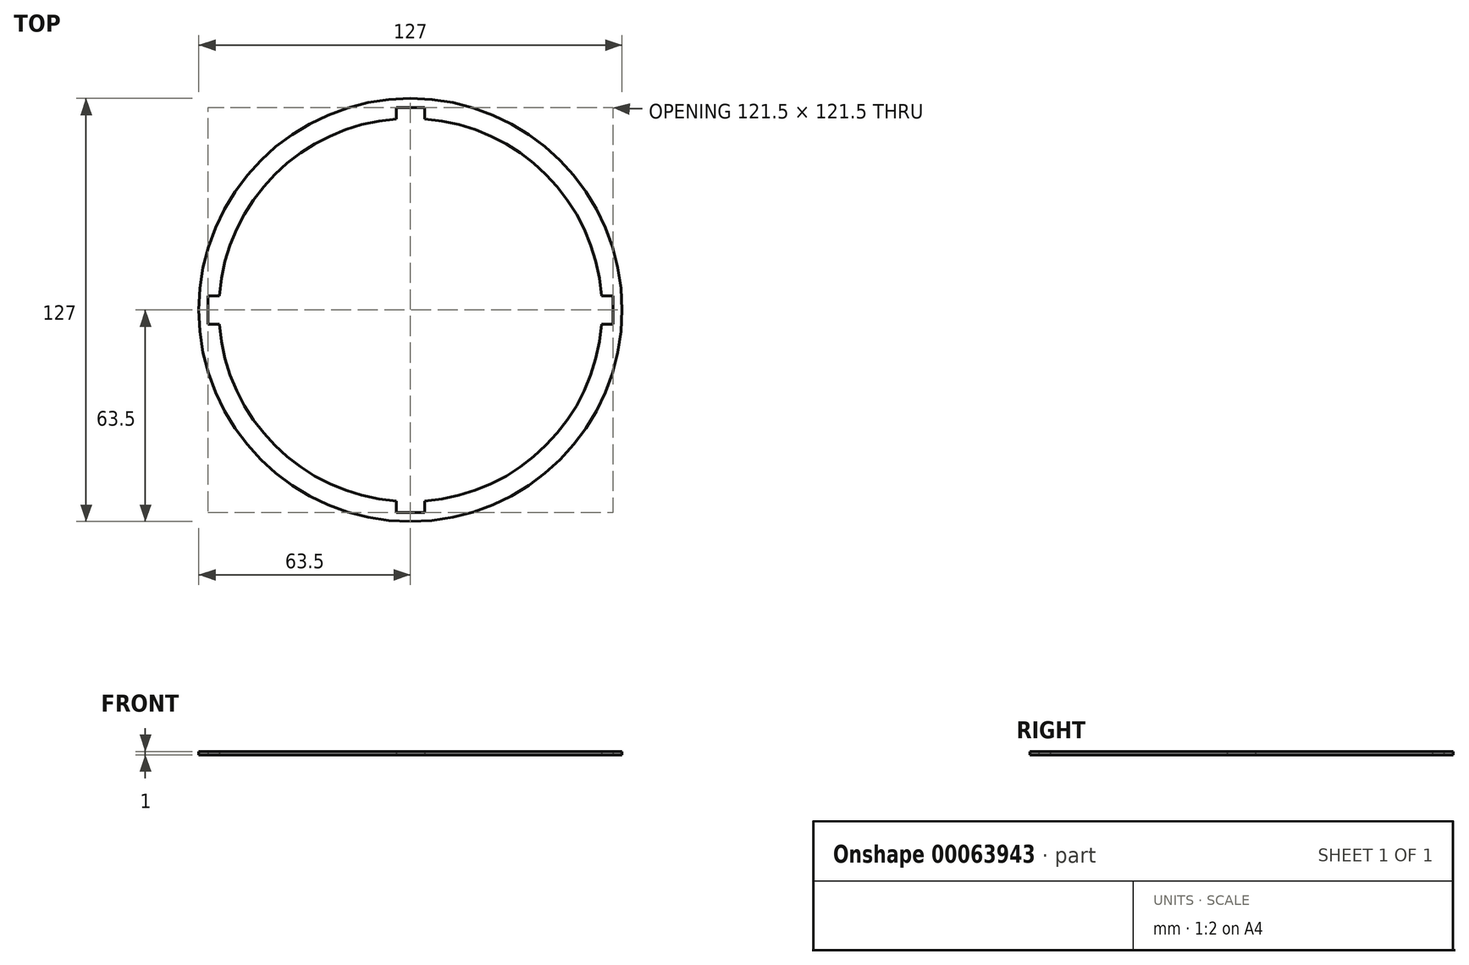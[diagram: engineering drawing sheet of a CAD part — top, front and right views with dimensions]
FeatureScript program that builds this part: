
annotation { "Feature Type Name" : "Feature", "Feature Type Description" : "" }
export const myFeature = defineFeature(function(context is Context, id is Id, definition is map)
    precondition{}
    {
        {
            var Q0;
            Q0=qCreatedBy(makeId("Top.planeOp"),FACE);
            var sketch = newSketch(context, id + "F0", { "sketchPlane" : qUnion([Q0])});
            skCircle(sketch, "E0", {"center": v(0, 0) * mm, "radius": 57.5 * mm});
            skCircle(sketch, "E1", {"center": v(0, 0) * mm, "radius": 63.5 * mm});
            skSolve(sketch);
        }
        {
            var Q0;
            Q0=makeQuery(id+"F0.imprint","IMPRINT",FACE,{"disambiguationData":[TD([[makeQuery(id+"F0.imprint","IMPRINT",EDGE,{"derivedFrom":sQuery(id+"F0.wireOp",EDGE,"E0")}),-1.0]])]});
            extrude(context, id + "F1", {"entities" : qUnion([Q0]), "depth" : 1 * mm});
        }
        {
            var Q0;
            Q0=qCreatedBy(makeId("Top.planeOp"),FACE);
            var sketch = newSketch(context, id + "F2", { "sketchPlane" : qUnion([Q0])});
            skLineSegment(sketch, "E2", {"start": v(0, 60.75) * mm, "end": v(-4.25, 60.75) * mm});
            skLineSegment(sketch, "E3", {"start": v(-4.25, 60.75) * mm, "end": v(-4.25, 56.5) * mm});
            skLineSegment(sketch, "E4", {"start": v(-4.25, 56.5) * mm, "end": v(4.25, 56.5) * mm});
            skLineSegment(sketch, "E5", {"start": v(4.25, 56.5) * mm, "end": v(4.25, 60.75) * mm});
            skLineSegment(sketch, "E6", {"start": v(0, 60.75) * mm, "end": v(4.25, 60.75) * mm});
            skLineSegment(sketch, "E7.MirrorCS", {"start": v(0, -60.75) * mm, "end": v(4.25, -60.75) * mm});
            skLineSegment(sketch, "E8.MirrorCS", {"start": v(0, -60.75) * mm, "end": v(-4.25, -60.75) * mm});
            skLineSegment(sketch, "E9.MirrorCS", {"start": v(4.25, -56.5) * mm, "end": v(4.25, -60.75) * mm});
            skLineSegment(sketch, "E10.MirrorCS", {"start": v(-4.25, -60.75) * mm, "end": v(-4.25, -56.5) * mm});
            skLineSegment(sketch, "E11.MirrorCS", {"start": v(-4.25, -56.5) * mm, "end": v(4.25, -56.5) * mm});
            skLineSegment(sketch, "E12", {"start": v(-60.75, 0) * mm, "end": v(-60.75, 4.25) * mm});
            skLineSegment(sketch, "E13", {"start": v(-60.75, 4.25) * mm, "end": v(-56.5, 4.25) * mm});
            skLineSegment(sketch, "E14", {"start": v(-56.5, 4.25) * mm, "end": v(-56.5, -4.25) * mm});
            skLineSegment(sketch, "E15", {"start": v(-56.5, -4.25) * mm, "end": v(-60.75, -4.25) * mm});
            skLineSegment(sketch, "E16", {"start": v(-60.75, 0) * mm, "end": v(-60.75, -4.25) * mm});
            skPoint(sketch, "E17.orphan", {"position": v(-60.68, -4.25) * mm});
            skLineSegment(sketch, "E18.MirrorCS", {"start": v(60.75, 0) * mm, "end": v(60.75, 4.25) * mm});
            skLineSegment(sketch, "E19.MirrorCS", {"start": v(60.75, 0) * mm, "end": v(60.75, -4.25) * mm});
            skLineSegment(sketch, "E20.MirrorCS", {"start": v(56.5, -4.25) * mm, "end": v(60.75, -4.25) * mm});
            skLineSegment(sketch, "E21.MirrorCS", {"start": v(56.5, 4.25) * mm, "end": v(56.5, -4.25) * mm});
            skLineSegment(sketch, "E22.MirrorCS", {"start": v(60.75, 4.25) * mm, "end": v(56.5, 4.25) * mm});
            skPoint(sketch, "E23.MirrorP", {"position": v(60.68, -4.25) * mm});
            skSolve(sketch);
        }
        {
            var Q0;
            Q0=qSketchRegion(id+"F2",true);
            extrude(context, id + "F3", {"entities" : qUnion([Q0]), "operationType" : NewBodyOperationType.REMOVE, "depth" : 25 * mm});
        }
    });
